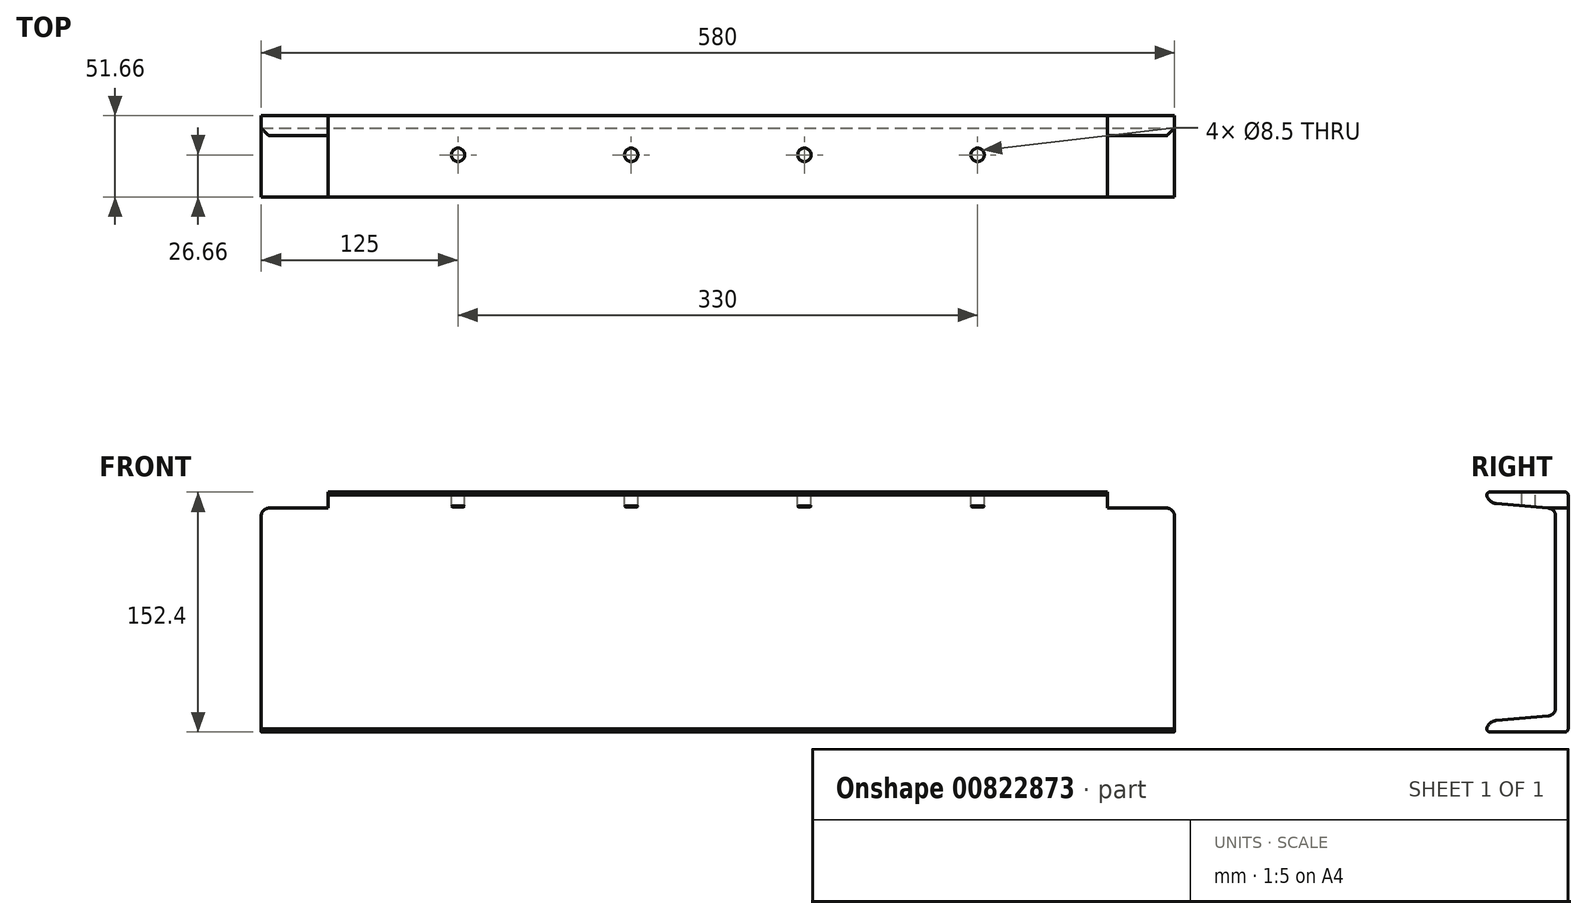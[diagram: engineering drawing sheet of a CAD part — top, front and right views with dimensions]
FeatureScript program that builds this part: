
annotation { "Feature Type Name" : "Feature", "Feature Type Description" : "" }
export const myFeature = defineFeature(function(context is Context, id is Id, definition is map)
    precondition{}
    {
        {
            var Q0;
            Q0=qCreatedBy(makeId("Right.planeOp"),FACE);
            var sketch = newSketch(context, id + "F0", { "sketchPlane" : qUnion([Q0])});
            skLineSegment(sketch, "E0.bottom", {"start": v(-23.83, -76.2) * mm, "end": v(23.83, -76.2) * mm});
            skLineSegment(sketch, "E0.top", {"start": v(-23.83, 76.2) * mm, "end": v(23.83, 76.2) * mm});
            skLineSegment(sketch, "E0.left", {"start": v(-25.83, -69.4) * mm, "end": v(-25.83, 69.4) * mm, "construction": true});
            skLineSegment(sketch, "E0.right", {"start": v(25.83, -74.2) * mm, "end": v(25.83, 74.2) * mm});
            skPoint(sketch, "E0.middle", {"position": v(0, 0) * mm});
            skLineSegment(sketch, "E1", {"start": v(-25.83, -69.4) * mm, "end": v(13.29, -65.98) * mm});
            skLineSegment(sketch, "E2", {"start": v(17.85, -61) * mm, "end": v(17.85, 61) * mm});
            skLineSegment(sketch, "E3", {"start": v(13.29, 65.98) * mm, "end": v(-25.83, 69.4) * mm});
            skLineSegment(sketch, "E4", {"start": v(-25.83, 69.4) * mm, "end": v(-25.83, 74.2) * mm});
            skLineSegment(sketch, "E5", {"start": v(-25.83, -69.4) * mm, "end": v(-25.83, -74.2) * mm});
            skPoint(sketch, "E6", {"position": v(-4, -67.49) * mm});
            skPoint(sketch, "E7", {"position": v(-3.99, 67.5) * mm});
            skPoint(sketch, "E8.visualSharp", {"position": v(25.83, 76.2) * mm});
            skArc(sketch, "E8.filletArc", {"start": v(25.83, 74.2) * mm, "mid": v(25.24, 75.61) * mm, "end": v(23.83, 76.2) * mm});
            skPoint(sketch, "E9.visualSharp", {"position": v(25.83, -76.2) * mm});
            skArc(sketch, "E9.filletArc", {"start": v(23.83, -76.2) * mm, "mid": v(25.24, -75.61) * mm, "end": v(25.83, -74.2) * mm});
            skPoint(sketch, "E10.visualSharp", {"position": v(-25.83, 76.2) * mm});
            skArc(sketch, "E10.filletArc", {"start": v(-23.83, 76.2) * mm, "mid": v(-25.24, 75.61) * mm, "end": v(-25.83, 74.2) * mm});
            skPoint(sketch, "E11.visualSharp", {"position": v(-25.83, -76.2) * mm});
            skArc(sketch, "E11.filletArc", {"start": v(-25.83, -74.2) * mm, "mid": v(-25.24, -75.61) * mm, "end": v(-23.83, -76.2) * mm});
            skPoint(sketch, "E12.visualSharp", {"position": v(17.85, -65.58) * mm});
            skArc(sketch, "E12.filletArc", {"start": v(13.29, -65.98) * mm, "mid": v(16.54, -64.38) * mm, "end": v(17.85, -61) * mm});
            skPoint(sketch, "E13.visualSharp", {"position": v(17.85, 65.58) * mm});
            skArc(sketch, "E13.filletArc", {"start": v(17.85, 61) * mm, "mid": v(16.54, 64.38) * mm, "end": v(13.29, 65.98) * mm});
            skSolve(sketch);
        }
        {
            var Q0;
            Q0=qSketchRegion(id+"F0",true);
            extrude(context, id + "F1", {"entities" : qUnion([Q0]), "endBound" : BoundingType.SYMMETRIC, "oppositeDirection" : true, "depth" : 580 * mm, "offsetDistance" : 25 * mm});
        }
        {
            var Q0;
            Q0=makeQuery(id+"F1.opExtrude","SWEPT_EDGE",EDGE,{"disambiguationData":[OSD([sQuery(id+"F0.wireOp",EDGE,"E1"),sQuery(id+"F0.wireOp",EDGE,"E5")])]});
            var Q1;
            Q1=makeQuery(id+"F1.opExtrude","SWEPT_EDGE",EDGE,{"disambiguationData":[OSD([sQuery(id+"F0.wireOp",EDGE,"E3"),sQuery(id+"F0.wireOp",EDGE,"E4")])]});
            fillet(context, id + "F2", {"entities" : qUnion([Q0, Q1]), "radius" : 7 * mm, "tangentPropagation" : true, "allowEdgeOverflow" : false});
        }
        {
            var Q0;
            Q0=makeQuery(id+"F1.opExtrude","SWEPT_FACE",FACE,{"disambiguationData":[OSD([sQuery(id+"F0.wireOp",EDGE,"E0.top")])]});
            var sketch = newSketch(context, id + "F3", { "sketchPlane" : qUnion([Q0])});
            skLineSegment(sketch, "E14.0", {"start": v(-290, 25.83) * mm, "end": v(290, 25.83) * mm, "construction": true});
            skLineSegment(sketch, "E15", {"start": v(-783.77, 0.83) * mm, "end": v(860.87, 0.83) * mm, "construction": true});
            skCircle(sketch, "E16", {"center": v(-275, 0.83) * mm, "radius": 4.25 * mm});
            skLineSegment(sketch, "E17.0", {"start": v(-290, -23.83) * mm, "end": v(-290, 23.83) * mm, "construction": true});
            skCircle(sketch, "E18.1.0.0", {"center": v(-165, 0.83) * mm, "radius": 4.25 * mm});
            skCircle(sketch, "E18.2.0.0", {"center": v(-55, 0.83) * mm, "radius": 4.25 * mm});
            skCircle(sketch, "E18.3.0.0", {"center": v(55, 0.83) * mm, "radius": 4.25 * mm});
            skCircle(sketch, "E18.4.0.0", {"center": v(165, 0.83) * mm, "radius": 4.25 * mm});
            skCircle(sketch, "E18.5.0.0", {"center": v(275, 0.83) * mm, "radius": 4.25 * mm});
            skLineSegment(sketch, "E18.direction1", {"start": v(-275, 0.83) * mm, "end": v(-165, 0.83) * mm, "construction": true});
            skSolve(sketch);
        }
        {
            var Q0;
            Q0=qSketchRegion(id+"F3",true);
            extrude(context, id + "F4", {"entities" : qUnion([Q0]), "operationType" : NewBodyOperationType.REMOVE, "oppositeDirection" : true, "depth" : 25 * mm, "offsetDistance" : 25 * mm});
        }
        {
            var Q0;
            Q0=makeQuery(id+"F1.opExtrude","SWEPT_FACE",FACE,{"disambiguationData":[OSD([sQuery(id+"F0.wireOp",EDGE,"E0.top")])]});
            var sketch = newSketch(context, id + "F5", { "sketchPlane" : qUnion([Q0])});
            skLineSegment(sketch, "E19.0", {"start": v(-290, -23.83) * mm, "end": v(-290, 23.83) * mm, "construction": true});
            skLineSegment(sketch, "E20.0", {"start": v(290, -23.83) * mm, "end": v(290, 23.83) * mm, "construction": true});
            skLineSegment(sketch, "E21", {"start": v(0, 0) * mm, "end": v(0, 74.15) * mm, "construction": true});
            skLineSegment(sketch, "E22", {"start": v(0, 74.15) * mm, "end": v(-247.5, 74.15) * mm, "construction": true});
            skLineSegment(sketch, "E23.bottom", {"start": v(-247.5, 74.15) * mm, "end": v(-307.5, 74.15) * mm});
            skLineSegment(sketch, "E23.top", {"start": v(-247.5, -56.7) * mm, "end": v(-307.5, -56.7) * mm});
            skLineSegment(sketch, "E23.left", {"start": v(-247.5, 74.15) * mm, "end": v(-247.5, -56.7) * mm});
            skLineSegment(sketch, "E23.right", {"start": v(-307.5, 74.15) * mm, "end": v(-307.5, -56.7) * mm});
            skLineSegment(sketch, "E24.MirrorCS", {"start": v(247.5, 74.15) * mm, "end": v(247.5, -56.7) * mm});
            skLineSegment(sketch, "E25.MirrorCS", {"start": v(307.5, 74.15) * mm, "end": v(307.5, -56.7) * mm});
            skLineSegment(sketch, "E26.MirrorCS", {"start": v(247.5, 74.15) * mm, "end": v(307.5, 74.15) * mm});
            skLineSegment(sketch, "E27.MirrorCS", {"start": v(247.5, -56.7) * mm, "end": v(307.5, -56.7) * mm});
            skSolve(sketch);
        }
        {
            var Q0;
            Q0 = qSketchRegion(id + "F5", true);
            extrude(context, id + "F6", {"entities" : qUnion([Q0]), "operationType" : NewBodyOperationType.REMOVE, "oppositeDirection" : true, "depth" : 10.2 * mm, "offsetDistance" : 25 * mm});
        }
        {
            var Q0;
            Q0=makeQuery(id+"F6.boolean.opBoolean","INTERSECT",EDGE,{"derivedFrom":[makeQuery(id+"F1.opExtrude","CAP_FACE",FACE,{"disambiguationData":[OSD([sQuery(id+"F0.wireOp",EDGE,"E0.bottom"),sQuery(id+"F0.wireOp",EDGE,"E0.top"),sQuery(id+"F0.wireOp",EDGE,"E0.right"),sQuery(id+"F0.wireOp",EDGE,"E1"),sQuery(id+"F0.wireOp",EDGE,"E2"),sQuery(id+"F0.wireOp",EDGE,"E3"),sQuery(id+"F0.wireOp",EDGE,"E4"),sQuery(id+"F0.wireOp",EDGE,"E5"),sQuery(id+"F0.wireOp",EDGE,"E8.filletArc"),sQuery(id+"F0.wireOp",EDGE,"E9.filletArc"),sQuery(id+"F0.wireOp",EDGE,"E10.filletArc"),sQuery(id+"F0.wireOp",EDGE,"E11.filletArc"),sQuery(id+"F0.wireOp",EDGE,"E12.filletArc"),sQuery(id+"F0.wireOp",EDGE,"E13.filletArc")])],"isStart":false}),makeQuery(id+"F6.opExtrude","CAP_FACE",FACE,{"disambiguationData":[OSD([sQuery(id+"F5.wireOp",EDGE,"E23.bottom"),sQuery(id+"F5.wireOp",EDGE,"E23.top"),sQuery(id+"F5.wireOp",EDGE,"E23.left"),sQuery(id+"F5.wireOp",EDGE,"E23.right")])],"isStart":false})]});
            var Q1;
            Q1=makeQuery(id+"FTmG2pmHad1P8ao_1.1.F6.boolean.opBoolean","INTERSECT",EDGE,{"derivedFrom":[makeQuery(id+"F1.opExtrude","CAP_FACE",FACE,{"disambiguationData":[OSD([sQuery(id+"F0.wireOp",EDGE,"E0.bottom"),sQuery(id+"F0.wireOp",EDGE,"E0.top"),sQuery(id+"F0.wireOp",EDGE,"E0.right"),sQuery(id+"F0.wireOp",EDGE,"E1"),sQuery(id+"F0.wireOp",EDGE,"E2"),sQuery(id+"F0.wireOp",EDGE,"E3"),sQuery(id+"F0.wireOp",EDGE,"E4"),sQuery(id+"F0.wireOp",EDGE,"E5"),sQuery(id+"F0.wireOp",EDGE,"E8.filletArc"),sQuery(id+"F0.wireOp",EDGE,"E9.filletArc"),sQuery(id+"F0.wireOp",EDGE,"E10.filletArc"),sQuery(id+"F0.wireOp",EDGE,"E11.filletArc"),sQuery(id+"F0.wireOp",EDGE,"E12.filletArc"),sQuery(id+"F0.wireOp",EDGE,"E13.filletArc")])],"isStart":false}),makeQuery(id+"FTmG2pmHad1P8ao_1.1.F6.opExtrude","CAP_FACE",FACE,{"disambiguationData":[OSD([sQuery(id+"F5.wireOp",EDGE,"E23.bottom"),sQuery(id+"F5.wireOp",EDGE,"E23.top"),sQuery(id+"F5.wireOp",EDGE,"E23.left"),sQuery(id+"F5.wireOp",EDGE,"E23.right")])],"isStart":false})]});
            var Q2;
            Q2=makeQuery(id+"F6.boolean.opBoolean","INTERSECT",EDGE,{"derivedFrom":[makeQuery(id+"F1.opExtrude","CAP_FACE",FACE,{"disambiguationData":[OSD([sQuery(id+"F0.wireOp",EDGE,"E0.bottom"),sQuery(id+"F0.wireOp",EDGE,"E0.top"),sQuery(id+"F0.wireOp",EDGE,"E0.right"),sQuery(id+"F0.wireOp",EDGE,"E1"),sQuery(id+"F0.wireOp",EDGE,"E2"),sQuery(id+"F0.wireOp",EDGE,"E3"),sQuery(id+"F0.wireOp",EDGE,"E4"),sQuery(id+"F0.wireOp",EDGE,"E5"),sQuery(id+"F0.wireOp",EDGE,"E8.filletArc"),sQuery(id+"F0.wireOp",EDGE,"E9.filletArc"),sQuery(id+"F0.wireOp",EDGE,"E10.filletArc"),sQuery(id+"F0.wireOp",EDGE,"E11.filletArc"),sQuery(id+"F0.wireOp",EDGE,"E12.filletArc"),sQuery(id+"F0.wireOp",EDGE,"E13.filletArc")])],"isStart":true}),makeQuery(id+"F6.opExtrude","CAP_FACE",FACE,{"disambiguationData":[OSD([sQuery(id+"F5.wireOp",EDGE,"E24.MirrorCS"),sQuery(id+"F5.wireOp",EDGE,"E25.MirrorCS"),sQuery(id+"F5.wireOp",EDGE,"E26.MirrorCS"),sQuery(id+"F5.wireOp",EDGE,"E27.MirrorCS")])],"isStart":false})]});
            var Q3;
            Q3=makeQuery(id+"FTmG2pmHad1P8ao_1.1.F6.boolean.opBoolean","INTERSECT",EDGE,{"derivedFrom":[makeQuery(id+"F1.opExtrude","CAP_FACE",FACE,{"disambiguationData":[OSD([sQuery(id+"F0.wireOp",EDGE,"E0.bottom"),sQuery(id+"F0.wireOp",EDGE,"E0.top"),sQuery(id+"F0.wireOp",EDGE,"E0.right"),sQuery(id+"F0.wireOp",EDGE,"E1"),sQuery(id+"F0.wireOp",EDGE,"E2"),sQuery(id+"F0.wireOp",EDGE,"E3"),sQuery(id+"F0.wireOp",EDGE,"E4"),sQuery(id+"F0.wireOp",EDGE,"E5"),sQuery(id+"F0.wireOp",EDGE,"E8.filletArc"),sQuery(id+"F0.wireOp",EDGE,"E9.filletArc"),sQuery(id+"F0.wireOp",EDGE,"E10.filletArc"),sQuery(id+"F0.wireOp",EDGE,"E11.filletArc"),sQuery(id+"F0.wireOp",EDGE,"E12.filletArc"),sQuery(id+"F0.wireOp",EDGE,"E13.filletArc")])],"isStart":true}),makeQuery(id+"FTmG2pmHad1P8ao_1.1.F6.opExtrude","CAP_FACE",FACE,{"disambiguationData":[OSD([sQuery(id+"F5.wireOp",EDGE,"E24.MirrorCS"),sQuery(id+"F5.wireOp",EDGE,"E25.MirrorCS"),sQuery(id+"F5.wireOp",EDGE,"E26.MirrorCS"),sQuery(id+"F5.wireOp",EDGE,"E27.MirrorCS")])],"isStart":false})]});
            fillet(context, id + "F7", {"entities" : qUnion([Q0, Q1, Q2, Q3]), "radius" : 5 * mm, "tangentPropagation" : true, "allowEdgeOverflow" : false});
        }
    });
